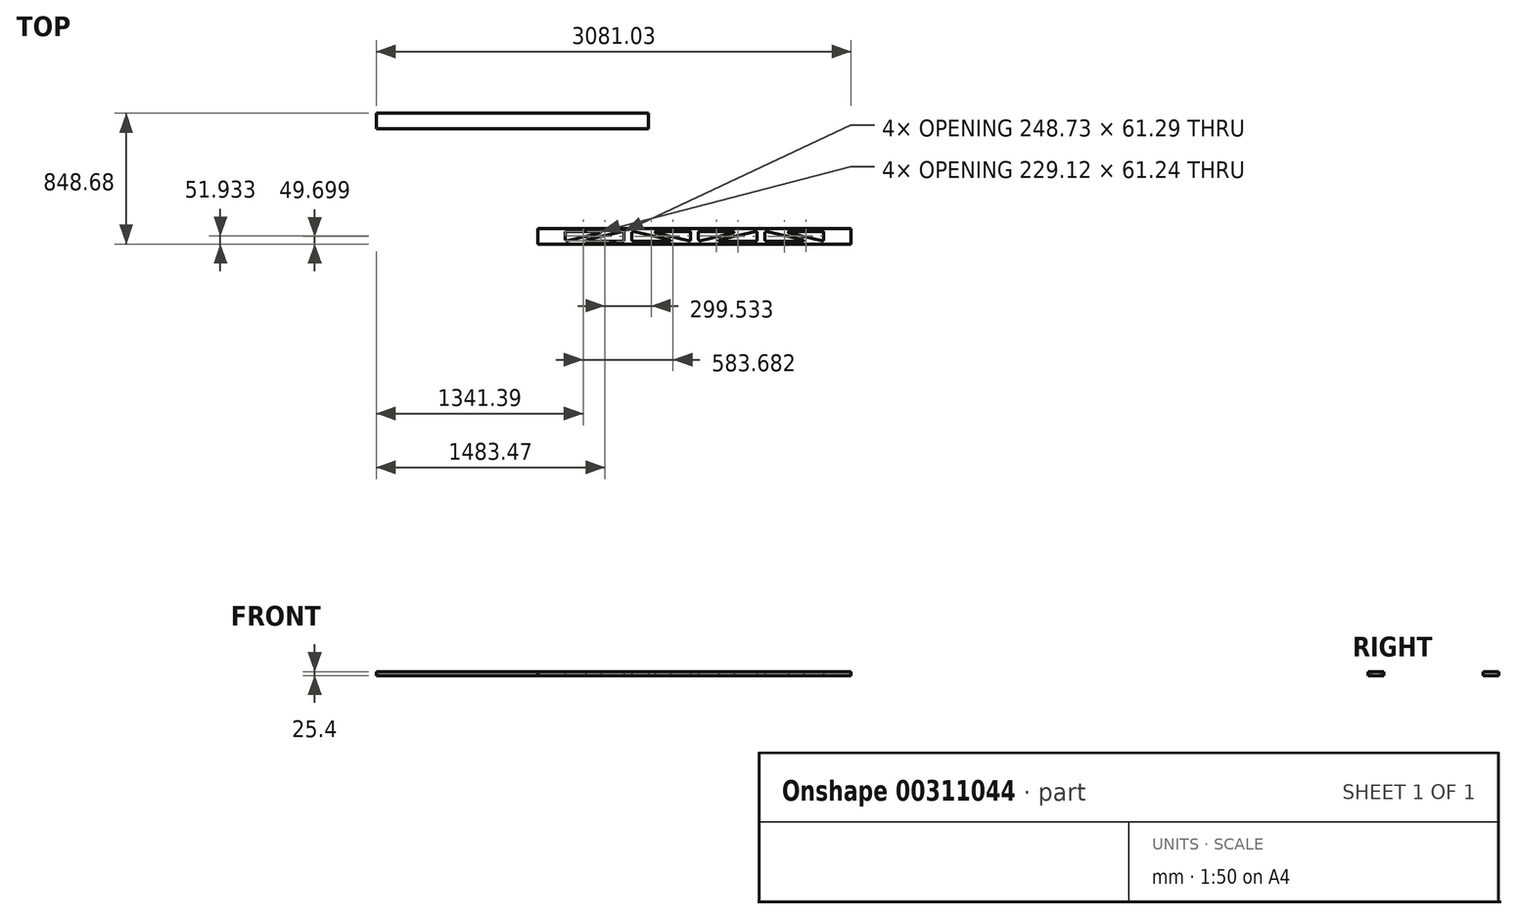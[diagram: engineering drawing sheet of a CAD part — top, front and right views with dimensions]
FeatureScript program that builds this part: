
annotation { "Feature Type Name" : "Feature", "Feature Type Description" : "" }
export const myFeature = defineFeature(function(context is Context, id is Id, definition is map)
    precondition{}
    {
        {
            var Q0;
            Q0=qCreatedBy(makeId("Top.planeOp"),FACE);
            var sketch = newSketch(context, id + "F0", { "sketchPlane" : qUnion([Q0])});
            skLineSegment(sketch, "E0.bottom", {"start": v(-1022.2, 52.33) * mm, "end": v(1009.8, 52.33) * mm});
            skLineSegment(sketch, "E0.top", {"start": v(-1022.2, -49.27) * mm, "end": v(1009.8, -49.27) * mm});
            skLineSegment(sketch, "E0.left", {"start": v(-1022.2, 52.33) * mm, "end": v(-1022.2, -49.27) * mm});
            skLineSegment(sketch, "E0.right", {"start": v(1009.8, 52.33) * mm, "end": v(1009.8, -49.27) * mm});
            skLineSegment(sketch, "E1", {"start": v(-6.2, 52.33) * mm, "end": v(-6.2, -49.27) * mm, "construction": true});
            skLineSegment(sketch, "E2", {"start": v(19.2, 26.93) * mm, "end": v(19.2, -19.02) * mm});
            skLineSegment(sketch, "E3", {"start": v(25.55, 33.28) * mm, "end": v(242.01, 33.28) * mm});
            skLineSegment(sketch, "E4", {"start": v(243.42, 20.74) * mm, "end": v(30.12, -27.74) * mm});
            skLineSegment(sketch, "E5", {"start": v(400.2, 22.34) * mm, "end": v(400.2, -23.87) * mm});
            skLineSegment(sketch, "E6", {"start": v(393.85, -30.22) * mm, "end": v(155.32, -30.22) * mm});
            skLineSegment(sketch, "E7", {"start": v(154.46, -22.57) * mm, "end": v(389.53, 30.86) * mm});
            skPoint(sketch, "E8.visualSharp", {"position": v(19.2, 33.28) * mm});
            skArc(sketch, "E8.filletArc", {"start": v(25.55, 33.28) * mm, "mid": v(21.06, 31.42) * mm, "end": v(19.2, 26.93) * mm});
            skPoint(sketch, "E9.visualSharp", {"position": v(19.2, -30.22) * mm});
            skArc(sketch, "E9.filletArc", {"start": v(19.31, -17.63) * mm, "mid": v(22.04, -25.55) * mm, "end": v(30.12, -27.74) * mm});
            skArc(sketch, "E10.filletArc", {"start": v(19.2, -19.02) * mm, "mid": v(22.57, -26) * mm, "end": v(30.12, -27.74) * mm});
            skPoint(sketch, "E11.visualSharp", {"position": v(298.6, 33.28) * mm});
            skArc(sketch, "E11.filletArc", {"start": v(243.42, 20.74) * mm, "mid": v(248.32, 27.64) * mm, "end": v(242.01, 33.28) * mm});
            skPoint(sketch, "E12.visualSharp", {"position": v(400.2, 33.28) * mm});
            skArc(sketch, "E12.filletArc", {"start": v(400.2, 22.34) * mm, "mid": v(396.92, 29.17) * mm, "end": v(389.53, 30.86) * mm});
            skPoint(sketch, "E13.visualSharp", {"position": v(400.2, -30.22) * mm});
            skArc(sketch, "E13.filletArc", {"start": v(393.85, -30.22) * mm, "mid": v(398.35, -28.36) * mm, "end": v(400.2, -23.87) * mm});
            skPoint(sketch, "E14.visualSharp", {"position": v(120.8, -30.22) * mm});
            skArc(sketch, "E14.filletArc", {"start": v(154.46, -22.57) * mm, "mid": v(151.47, -26.78) * mm, "end": v(155.32, -30.22) * mm});
            skLineSegment(sketch, "E15", {"start": v(425.6, 52.33) * mm, "end": v(425.6, -49.27) * mm, "construction": true});
            skArc(sketch, "E16.MirrorCS", {"start": v(832, -19.02) * mm, "mid": v(828.64, -26) * mm, "end": v(821.09, -27.74) * mm});
            skArc(sketch, "E17.MirrorCS", {"start": v(825.65, 33.28) * mm, "mid": v(830.15, 31.42) * mm, "end": v(832, 26.93) * mm});
            skArc(sketch, "E18.MirrorCS", {"start": v(457.35, -30.22) * mm, "mid": v(452.86, -28.36) * mm, "end": v(451, -23.87) * mm});
            skArc(sketch, "E19.MirrorCS", {"start": v(696.75, -22.57) * mm, "mid": v(699.74, -26.78) * mm, "end": v(695.89, -30.22) * mm});
            skArc(sketch, "E20.MirrorCS", {"start": v(831.9, -17.63) * mm, "mid": v(829.17, -25.55) * mm, "end": v(821.09, -27.74) * mm});
            skArc(sketch, "E21.MirrorCS", {"start": v(607.8, 20.74) * mm, "mid": v(602.89, 27.64) * mm, "end": v(609.2, 33.28) * mm});
            skArc(sketch, "E22.MirrorCS", {"start": v(451, 22.34) * mm, "mid": v(454.3, 29.17) * mm, "end": v(461.68, 30.86) * mm});
            skPoint(sketch, "E23.MirrorP", {"position": v(552.6, 33.28) * mm});
            skLineSegment(sketch, "E24.MirrorCS", {"start": v(832, 26.93) * mm, "end": v(832, -19.02) * mm});
            skPoint(sketch, "E25.MirrorP", {"position": v(832, -30.22) * mm});
            skLineSegment(sketch, "E26.MirrorCS", {"start": v(825.65, 33.28) * mm, "end": v(609.2, 33.28) * mm});
            skLineSegment(sketch, "E27.MirrorCS", {"start": v(607.8, 20.74) * mm, "end": v(821.09, -27.74) * mm});
            skLineSegment(sketch, "E28.MirrorCS", {"start": v(451, 22.34) * mm, "end": v(451, -23.87) * mm});
            skLineSegment(sketch, "E29.MirrorCS", {"start": v(457.35, -30.22) * mm, "end": v(695.89, -30.22) * mm});
            skLineSegment(sketch, "E30.MirrorCS", {"start": v(696.75, -22.57) * mm, "end": v(461.68, 30.86) * mm});
            skPoint(sketch, "E31.MirrorP", {"position": v(451, -30.22) * mm});
            skPoint(sketch, "E32.MirrorP", {"position": v(832, 33.28) * mm});
            skPoint(sketch, "E33.MirrorP", {"position": v(451, 33.28) * mm});
            skPoint(sketch, "E34.MirrorP", {"position": v(730.4, -30.22) * mm});
            skArc(sketch, "E35.MirrorCS", {"start": v(-469.75, -30.22) * mm, "mid": v(-465.25, -28.36) * mm, "end": v(-463.4, -23.87) * mm});
            skArc(sketch, "E36.MirrorCS", {"start": v(-844.4, -19.02) * mm, "mid": v(-841.03, -26) * mm, "end": v(-833.48, -27.74) * mm});
            skArc(sketch, "E37.MirrorCS", {"start": v(-37.95, 33.28) * mm, "mid": v(-33.45, 31.42) * mm, "end": v(-31.6, 26.93) * mm});
            skArc(sketch, "E38.MirrorCS", {"start": v(-166.85, -22.57) * mm, "mid": v(-163.86, -26.78) * mm, "end": v(-167.71, -30.22) * mm});
            skArc(sketch, "E39.MirrorCS", {"start": v(-709.14, -22.57) * mm, "mid": v(-712.13, -26.78) * mm, "end": v(-708.28, -30.22) * mm});
            skArc(sketch, "E40.MirrorCS", {"start": v(-844.29, -17.63) * mm, "mid": v(-841.56, -25.55) * mm, "end": v(-833.48, -27.74) * mm});
            skArc(sketch, "E41.MirrorCS", {"start": v(-406.25, -30.22) * mm, "mid": v(-410.74, -28.36) * mm, "end": v(-412.6, -23.87) * mm});
            skArc(sketch, "E42.MirrorCS", {"start": v(-838.05, 33.28) * mm, "mid": v(-842.54, 31.42) * mm, "end": v(-844.4, 26.93) * mm});
            skArc(sketch, "E43.MirrorCS", {"start": v(-31.7, -17.63) * mm, "mid": v(-34.43, -25.55) * mm, "end": v(-42.51, -27.74) * mm});
            skArc(sketch, "E44.MirrorCS", {"start": v(-31.6, -19.02) * mm, "mid": v(-34.96, -26) * mm, "end": v(-42.51, -27.74) * mm});
            skArc(sketch, "E45.MirrorCS", {"start": v(-620.18, 20.74) * mm, "mid": v(-615.28, 27.64) * mm, "end": v(-621.59, 33.28) * mm});
            skArc(sketch, "E46.MirrorCS", {"start": v(-463.4, 22.34) * mm, "mid": v(-466.68, 29.17) * mm, "end": v(-474.07, 30.86) * mm});
            skArc(sketch, "E47.MirrorCS", {"start": v(-412.6, 22.34) * mm, "mid": v(-409.3, 29.17) * mm, "end": v(-401.92, 30.86) * mm});
            skArc(sketch, "E48.MirrorCS", {"start": v(-255.8, 20.74) * mm, "mid": v(-260.71, 27.64) * mm, "end": v(-254.4, 33.28) * mm});
            skPoint(sketch, "E49.MirrorP", {"position": v(-844.4, -30.22) * mm});
            skLineSegment(sketch, "E50.MirrorCS", {"start": v(-620.18, 20.74) * mm, "end": v(-833.48, -27.74) * mm});
            skLineSegment(sketch, "E51.MirrorCS", {"start": v(-469.75, -30.22) * mm, "end": v(-708.28, -30.22) * mm});
            skPoint(sketch, "E52.MirrorP", {"position": v(-463.4, 33.28) * mm});
            skPoint(sketch, "E53.MirrorP", {"position": v(-565, 33.28) * mm});
            skPoint(sketch, "E54.MirrorP", {"position": v(-31.6, -30.22) * mm});
            skPoint(sketch, "E55.MirrorP", {"position": v(-463.4, -30.22) * mm});
            skLineSegment(sketch, "E56.MirrorCS", {"start": v(-709.14, -22.57) * mm, "end": v(-474.07, 30.86) * mm});
            skPoint(sketch, "E57.MirrorP", {"position": v(-742.8, -30.22) * mm});
            skPoint(sketch, "E58.MirrorP", {"position": v(-412.6, -30.22) * mm});
            skLineSegment(sketch, "E59.MirrorCS", {"start": v(-31.6, 26.93) * mm, "end": v(-31.6, -19.02) * mm});
            skPoint(sketch, "E60.MirrorP", {"position": v(-31.6, 33.28) * mm});
            skLineSegment(sketch, "E61.MirrorCS", {"start": v(-463.4, 22.34) * mm, "end": v(-463.4, -23.87) * mm});
            skLineSegment(sketch, "E62.MirrorCS", {"start": v(-406.25, -30.22) * mm, "end": v(-167.71, -30.22) * mm});
            skPoint(sketch, "E63.MirrorP", {"position": v(-311, 33.28) * mm});
            skLineSegment(sketch, "E64.MirrorCS", {"start": v(-838.05, 33.28) * mm, "end": v(-621.59, 33.28) * mm});
            skLineSegment(sketch, "E65.MirrorCS", {"start": v(-844.4, 26.93) * mm, "end": v(-844.4, -19.02) * mm});
            skPoint(sketch, "E66.MirrorP", {"position": v(-412.6, 33.28) * mm});
            skLineSegment(sketch, "E67.MirrorCS", {"start": v(-166.85, -22.57) * mm, "end": v(-401.92, 30.86) * mm});
            skPoint(sketch, "E68.MirrorP", {"position": v(-844.4, 33.28) * mm});
            skLineSegment(sketch, "E69.MirrorCS", {"start": v(-37.95, 33.28) * mm, "end": v(-254.4, 33.28) * mm});
            skPoint(sketch, "E70.MirrorP", {"position": v(-133.2, -30.22) * mm});
            skLineSegment(sketch, "E71.MirrorCS", {"start": v(-412.6, 22.34) * mm, "end": v(-412.6, -23.87) * mm});
            skLineSegment(sketch, "E72.MirrorCS", {"start": v(-255.8, 20.74) * mm, "end": v(-42.51, -27.74) * mm});
            skLineSegment(sketch, "E73.bottom", {"start": v(-2071.23, 799.41) * mm, "end": v(-305.93, 799.41) * mm});
            skLineSegment(sketch, "E73.top", {"start": v(-2071.23, 697.81) * mm, "end": v(-305.93, 697.81) * mm});
            skLineSegment(sketch, "E73.left", {"start": v(-2071.23, 799.41) * mm, "end": v(-2071.23, 697.81) * mm});
            skLineSegment(sketch, "E73.right", {"start": v(-305.93, 799.41) * mm, "end": v(-305.93, 697.81) * mm});
            skLineSegment(sketch, "E74", {"start": v(-1321.93, 799.41) * mm, "end": v(-1321.93, 697.81) * mm, "construction": true});
            skLineSegment(sketch, "E75", {"start": v(-890.13, 799.41) * mm, "end": v(-890.13, 697.81) * mm, "construction": true});
            skSolve(sketch);
        }
        {
            var Q0;
            Q0=makeQuery(id+"F0.imprint","IMPRINT",FACE,{"disambiguationData":[TD([[makeQuery(id+"F0.imprint","IMPRINT",EDGE,{"derivedFrom":sQuery(id+"F0.wireOp",EDGE,"E0.bottom")}),-1.0]])]});
            extrude(context, id + "F1", {"entities" : qUnion([Q0]), "depth" : 25.4 * mm});
        }
        {
            var Q0;
            Q0=makeQuery(id+"F0.imprint","IMPRINT",FACE,{"disambiguationData":[TD([[makeQuery(id+"F0.imprint","IMPRINT",EDGE,{"derivedFrom":sQuery(id+"F0.wireOp",EDGE,"E73.bottom")}),-1.0]])]});
            extrude(context, id + "F2", {"entities" : qUnion([Q0]), "depth" : 25.4 * mm});
        }
    });
